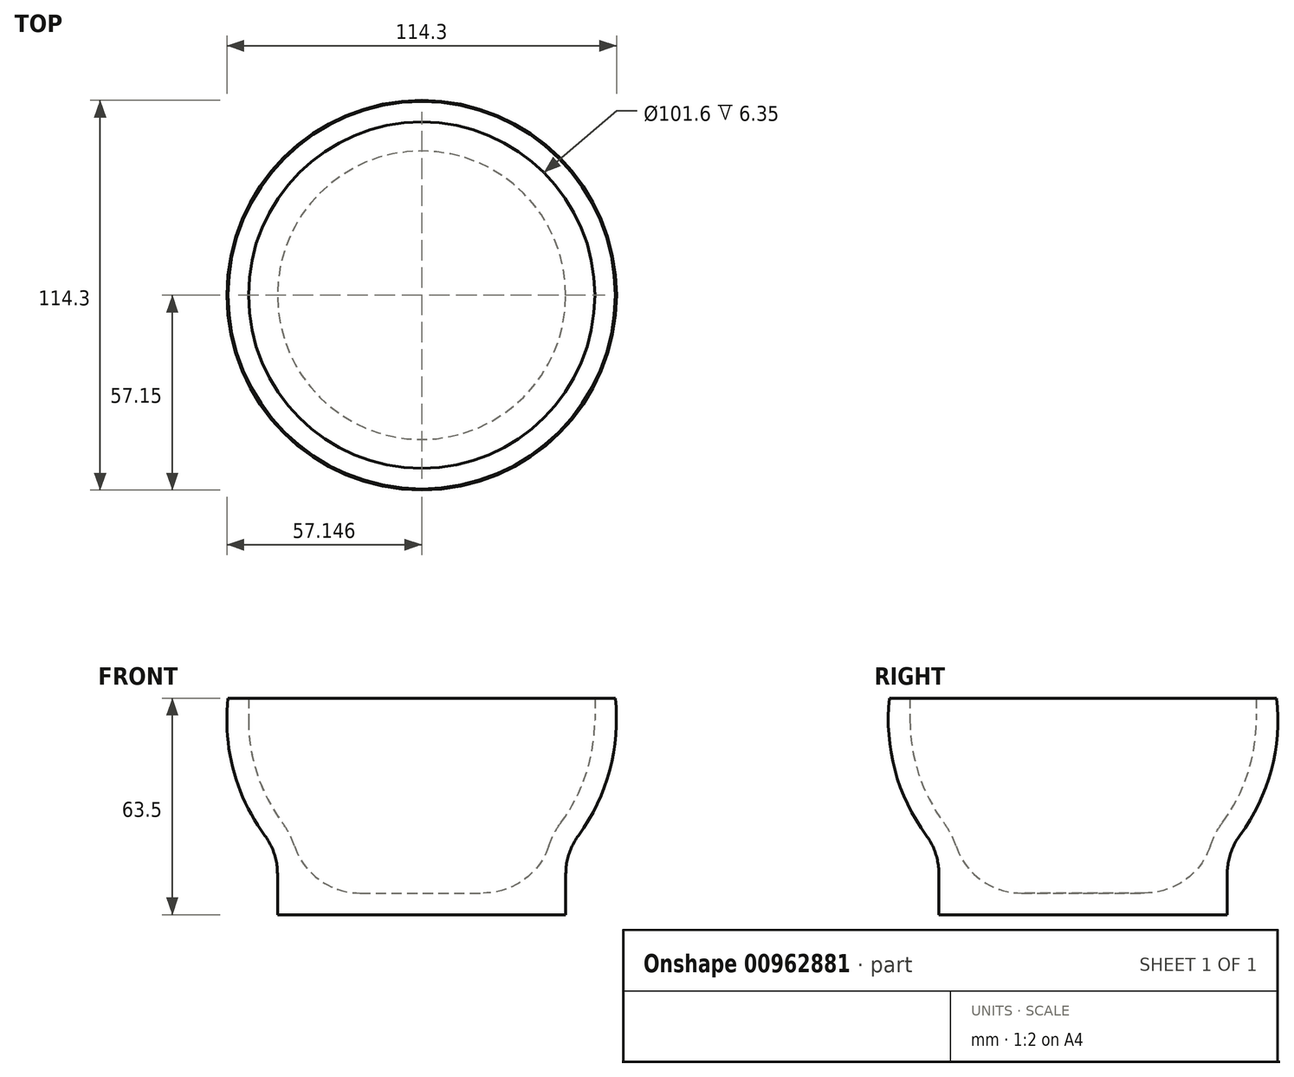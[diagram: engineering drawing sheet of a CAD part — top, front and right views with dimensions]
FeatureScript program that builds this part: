
annotation { "Feature Type Name" : "Feature", "Feature Type Description" : "" }
export const myFeature = defineFeature(function(context is Context, id is Id, definition is map)
    precondition{}
    {
        {
            var Q0;
            Q0=qCreatedBy(makeId("Front.planeOp"),FACE);
            var sketch = newSketch(context, id + "F0", { "sketchPlane" : qUnion([Q0])});
            skArc(sketch, "E0", {"start": v(-5.66, 34.56) * mm, "mid": v(1.71, 48.84) * mm, "end": v(4.26, 64.7) * mm});
            skLineSegment(sketch, "E1.bottom", {"start": v(-46.54, 13.9) * mm, "end": v(-28.5, 13.9) * mm});
            skPoint(sketch, "E2.visualSharp", {"position": v(-10.61, 28.8) * mm});
            skArc(sketch, "E2.filletArc", {"start": v(-5.66, 34.56) * mm, "mid": v(-7.72, 31.25) * mm, "end": v(-9.26, 27.67) * mm});
            skLineSegment(sketch, "E3.0", {"start": v(-46.54, 7.55) * mm, "end": v(-4.26, 7.55) * mm});
            skLineSegment(sketch, "E3.1", {"start": v(-4.26, 7.55) * mm, "end": v(-4.26, 19.49) * mm});
            skArc(sketch, "E3.3", {"start": v(-0.54, 30.8) * mm, "mid": v(-3.3, 25.44) * mm, "end": v(-4.26, 19.49) * mm});
            skArc(sketch, "E3.4", {"start": v(-0.54, 30.8) * mm, "mid": v(8.66, 49.9) * mm, "end": v(10.25, 71.05) * mm});
            skLineSegment(sketch, "E3.5", {"start": v(4.26, 71.05) * mm, "end": v(10.25, 71.05) * mm});
            skLineSegment(sketch, "E4", {"start": v(4.26, 64.7) * mm, "end": v(4.26, 71.05) * mm});
            skArc(sketch, "E5.filletArc", {"start": v(-28.5, 13.9) * mm, "mid": v(-16.66, 17.7) * mm, "end": v(-9.26, 27.67) * mm});
            skLineSegment(sketch, "E6", {"start": v(-46.54, 7.55) * mm, "end": v(-46.54, 13.9) * mm});
            skSolve(sketch);
        }
        {
            var Q0;
            Q0 = qSketchRegion(id + "F0", true);
            var Q1;
            Q1=sQuery(id+"F0.wireOp",EDGE,"E6");
            revolve(context, id + "F1", {"surfaceOperationType" : NewSurfaceOperationType.NEW, "entities" : qUnion([Q0]), "axis" : qUnion([Q1]), "revolveType" : RevolveType.FULL});
        }
    });
